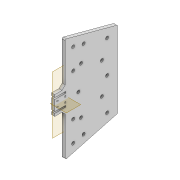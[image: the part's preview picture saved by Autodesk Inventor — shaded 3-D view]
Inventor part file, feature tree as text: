
AUTODESK INVENTOR PART (.ipt)
format: ipt  version: 2022 (Build 260153000, 153)  size: 328,192 bytes
history: native  units: mm
features: extrude x6, sketch x6, fillet x3, projected_geometry x3, plane x2, thicken_offset x2, mirror x1, chamfer x1
ambient origin geometry x8: Origin, YZ Plane, XZ Plane, XY Plane, X Axis, Y Axis, Z Axis, Center Point
bodies: Solid1 (feature_tree)
feature tree (24):
  extrude  "Extrusion1"  Depth=100.0mm
  extrude  "Extrusion2"  Depth=5.0mm
  plane  "Work Plane1"
  extrude  "Extrusion11"  Depth=10.0mm
  plane  "Work Plane3"
  thicken_offset  "Thicken1"
  thicken_offset  "Thicken2"
  extrude  "Extrusion12"  Depth=5.0mm
  extrude  "Extrusion13"  Depth=3.1mm
  mirror  "Mirror1"
  chamfer  "Chamfer1"  Distance=20.0mm
  fillet  "Fillet2"  Radius=3.0mm
  fillet  "Fillet3"  Radius=3.0mm
  extrude  "Extrusion14"  Depth=2.0mm
  fillet  "Fillet4"  Radius=3.0mm
  sketch  "Sketch1"  dims[d0=6.0mm d1=100.0mm]
  sketch  "Sketch3"  dims[d2=5.0mm d3=0.0mm d6=50.0mm]
  projected_geometry  "Projected Loop2"
  sketch  "Sketch13"  dims[d7=100.0mm d8=10.0mm]
  sketch  "Sketch14"  dims[d9=10.0mm d10=5.0mm]
  projected_geometry  "Projected Loop15"
  sketch  "Sketch15"  dims[d11=3.1mm d12=3.1mm]
  sketch  "Sketch19"  dims[d13=5.0mm d14=20.0mm d15=0.0mm d57=3.0mm d58=3.0mm d59=3.0mm d60=3.0mm d61=5.0mm d62=5.0mm d63=5.0mm d64=5.0mm d65=5.0mm d67=5.0mm d69=5.0mm d70=5.0mm d71=180.0mm d72=0.0mm d74=1.0mm d75=0.5mm d76=1.0mm d77=0.5mm d78=50.0mm d79=50.0mm d80=300.0mm d81=80.0mm d82=80.0mm d83=6.0mm d84=0.0mm d85=5.95mm d86=15.0mm d87=20.0mm d88=5.95mm d89=150.0mm d90=55.0mm d91=5.95mm d92=290.0mm d93=90.0mm d94=100.0mm d95=0.0mm d96=5.95mm d97=80.0mm d98=5.95mm d99=220.0mm d100=6.0mm d101=2.0mm d102=45.0deg d103=2.0mm d104=5.95mm d105=80.0mm d106=38.0mm d107=5.95mm d108=220.0mm d109=73.0mm d110=5.95mm d111=15.0mm d112=40.0mm d113=0.8mm d115=5.95mm d116=30.0mm d117=70.0mm d118=5.95mm d119=35.0mm d120=75.0mm d121=5.95mm d122=30.0mm d123=45.0mm d124=5.95mm d125=25.0mm d126=120.0mm d127=100.0mm d128=0.0mm d129=2.0mm]
  projected_geometry  "Projected Loop19"
